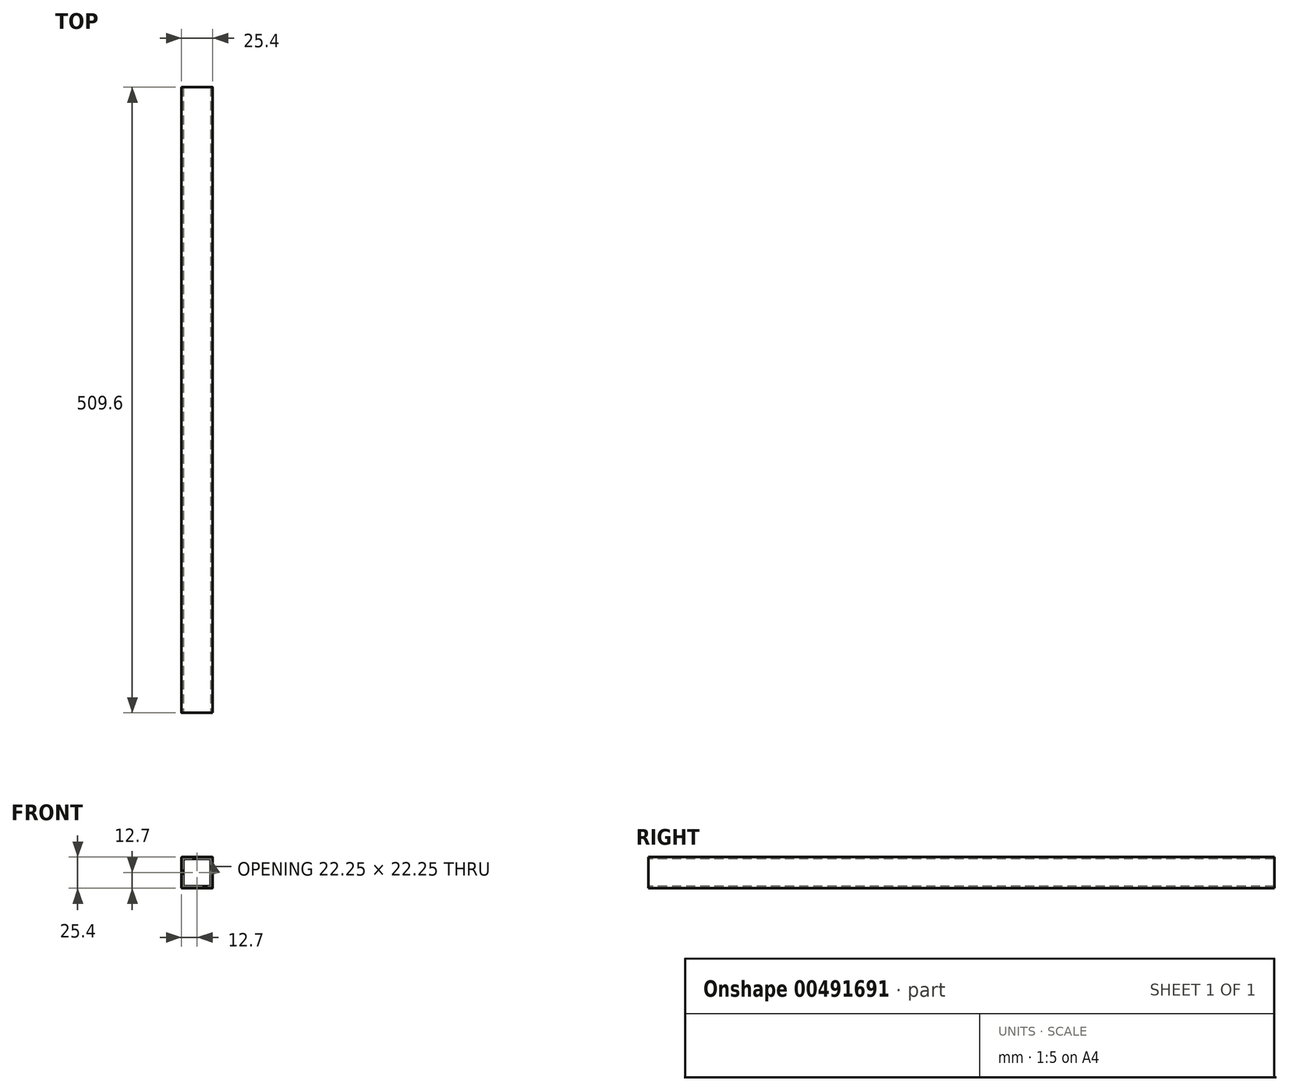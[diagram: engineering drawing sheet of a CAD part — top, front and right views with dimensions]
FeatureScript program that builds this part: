
annotation { "Feature Type Name" : "Feature", "Feature Type Description" : "" }
export const myFeature = defineFeature(function(context is Context, id is Id, definition is map)
    precondition{}
    {
        {
            var Q0;
            Q0=qCreatedBy(makeId("Front.planeOp"),FACE);
            var sketch = newSketch(context, id + "F0", { "sketchPlane" : qUnion([Q0])});
            skLineSegment(sketch, "E0.bottom", {"start": v(12.7, 12.7) * mm, "end": v(-12.7, 12.7) * mm});
            skLineSegment(sketch, "E0.top", {"start": v(12.7, -12.7) * mm, "end": v(-12.7, -12.7) * mm});
            skLineSegment(sketch, "E0.left", {"start": v(12.7, 12.7) * mm, "end": v(12.7, -12.7) * mm});
            skLineSegment(sketch, "E0.right", {"start": v(-12.7, 12.7) * mm, "end": v(-12.7, -12.7) * mm});
            skPoint(sketch, "E0.middle", {"position": v(0, 0) * mm});
            skSolve(sketch);
        }
        {
            var Q0;
            Q0=qSketchRegion(id+"F0",true);
            extrude(context, id + "F1", {"entities" : qUnion([Q0]), "depth" : 736.6 * mm});
        }
        {
            var Q0;
            Q0=makeQuery(id+"F1.opExtrude","CAP_FACE",FACE,{"disambiguationData":[OSD([sQuery(id+"F0.wireOp",EDGE,"E0.bottom"),sQuery(id+"F0.wireOp",EDGE,"E0.top"),sQuery(id+"F0.wireOp",EDGE,"E0.left"),sQuery(id+"F0.wireOp",EDGE,"E0.right")])],"isStart":false});
            var sketch = newSketch(context, id + "F2", { "sketchPlane" : qUnion([Q0])});
            skLineSegment(sketch, "E1.bottom", {"start": v(-11.13, 11.13) * mm, "end": v(11.13, 11.13) * mm});
            skLineSegment(sketch, "E1.top", {"start": v(-11.13, -11.13) * mm, "end": v(11.13, -11.13) * mm});
            skLineSegment(sketch, "E1.left", {"start": v(-11.13, 11.13) * mm, "end": v(-11.13, -11.13) * mm});
            skLineSegment(sketch, "E1.right", {"start": v(11.13, 11.13) * mm, "end": v(11.13, -11.13) * mm});
            skPoint(sketch, "E1.middle", {"position": v(0, 0) * mm});
            skSolve(sketch);
        }
        {
            var Q0;
            Q0=qSketchRegion(id+"F2",true);
            extrude(context, id + "F3", {"entities" : qUnion([Q0]), "operationType" : NewBodyOperationType.REMOVE, "endBound" : BoundingType.UP_TO_NEXT, "oppositeDirection" : true, "depth" : 25.4 * mm});
        }
        {
            var Q0;
            Q0=makeQuery(id+"F3.boolean.opBoolean","COPY",EDGE,{"derivedFrom":makeQuery(id+"F3.opExtrude","SWEPT_EDGE",EDGE,{"disambiguationData":[OSD([sQuery(id+"F2.wireOp",EDGE,"E1.bottom"),sQuery(id+"F2.wireOp",EDGE,"E1.left")])]})});
            var Q1;
            Q1=makeQuery(id+"F3.boolean.opBoolean","COPY",EDGE,{"derivedFrom":makeQuery(id+"F3.opExtrude","SWEPT_EDGE",EDGE,{"disambiguationData":[OSD([sQuery(id+"F2.wireOp",EDGE,"E1.top"),sQuery(id+"F2.wireOp",EDGE,"E1.right")])]})});
            var Q2;
            Q2=makeQuery(id+"F3.boolean.opBoolean","COPY",EDGE,{"derivedFrom":makeQuery(id+"F3.opExtrude","SWEPT_EDGE",EDGE,{"disambiguationData":[OSD([sQuery(id+"F2.wireOp",EDGE,"E1.bottom"),sQuery(id+"F2.wireOp",EDGE,"E1.right")])]})});
            var Q3;
            Q3=makeQuery(id+"F3.boolean.opBoolean","COPY",EDGE,{"derivedFrom":makeQuery(id+"F3.opExtrude","SWEPT_EDGE",EDGE,{"disambiguationData":[OSD([sQuery(id+"F2.wireOp",EDGE,"E1.top"),sQuery(id+"F2.wireOp",EDGE,"E1.left")])]})});
            fillet(context, id + "F4", {"entities" : qUnion([Q0, Q1, Q2, Q3]), "radius" : 1.52 * mm, "tangentPropagation" : true, "allowEdgeOverflow" : false});
        }
        {
            var Q0;
            Q0=makeQuery(id+"F1.opExtrude","SWEPT_EDGE",EDGE,{"disambiguationData":[OSD([sQuery(id+"F0.wireOp",EDGE,"E0.bottom"),sQuery(id+"F0.wireOp",EDGE,"E0.left")])]});
            var Q1;
            Q1=makeQuery(id+"F1.opExtrude","SWEPT_EDGE",EDGE,{"disambiguationData":[OSD([sQuery(id+"F0.wireOp",EDGE,"E0.top"),sQuery(id+"F0.wireOp",EDGE,"E0.left")])]});
            var Q2;
            Q2=makeQuery(id+"F1.opExtrude","SWEPT_EDGE",EDGE,{"disambiguationData":[OSD([sQuery(id+"F0.wireOp",EDGE,"E0.top"),sQuery(id+"F0.wireOp",EDGE,"E0.right")])]});
            var Q3;
            Q3=makeQuery(id+"F1.opExtrude","SWEPT_EDGE",EDGE,{"disambiguationData":[OSD([sQuery(id+"F0.wireOp",EDGE,"E0.bottom"),sQuery(id+"F0.wireOp",EDGE,"E0.right")])]});
            fillet(context, id + "F5", {"entities" : qUnion([Q0, Q1, Q2, Q3]), "radius" : 0.25 * mm, "tangentPropagation" : true, "allowEdgeOverflow" : false});
        }
        {
            var Q0;
            Q0=makeQuery(id+"F1.opExtrude","CAP_FACE",FACE,{"disambiguationData":[OSD([sQuery(id+"F0.wireOp",EDGE,"E0.bottom"),sQuery(id+"F0.wireOp",EDGE,"E0.top"),sQuery(id+"F0.wireOp",EDGE,"E0.left"),sQuery(id+"F0.wireOp",EDGE,"E0.right")])],"isStart":false});
            extrude(context, id + "F6", {"entities" : qUnion([Q0]), "operationType" : NewBodyOperationType.REMOVE, "oppositeDirection" : true, "depth" : 227 * mm});
        }
    });
